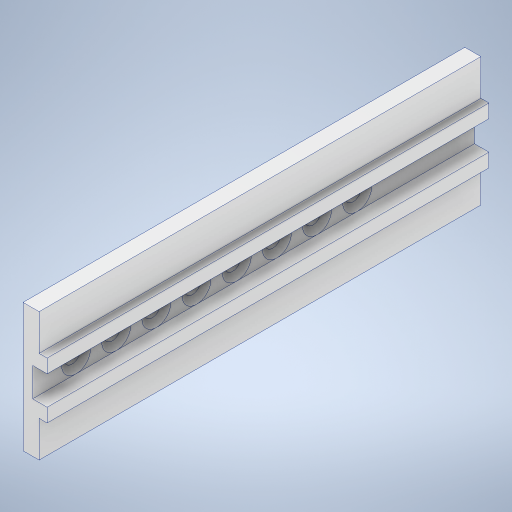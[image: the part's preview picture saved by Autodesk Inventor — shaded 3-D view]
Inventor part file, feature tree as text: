
AUTODESK INVENTOR PART (.ipt)
format: ipt  version: 2024 (Build 280153000, 153)  size: 330,240 bytes
history: native  units: mm
features: extrude x3, sketch x3, chamfer x1
ambient origin geometry x8: Origin, YZ Plane, XZ Plane, XY Plane, X Axis, Y Axis, Z Axis, Center Point
bodies: Solid1 (feature_tree)
feature tree (7):
  extrude  "Extrusion1"  Depth=160.0mm TaperAngle=0.0deg
  extrude  "Extrusion2"  Depth=25.0mm
  extrude  "Extrusion3"  Depth=45.0mm
  chamfer  "Chamfer1"  Distance=45.0mm
  sketch  "Sketch1"  dims[d0=550.0mm d1=160.0mm d2=0.0mm]
  sketch  "Sketch2"  dims[d4=25.0mm d5=25.0mm]
  sketch  "Sketch3"  dims[d6=10.0mm d7=45.0mm d8=45.0mm d9=18.0mm d10=36.0mm d11=80.0mm d12=80.0mm d13=150.0mm d14=0.0mm d15=30.0mm d16=90.0mm d18=50.0mm d19=10.0mm d21=10.0mm d23=25.0mm d24=0.0mm d25=8.0mm d26=5.0mm d27=45.0deg d28=39.130435mm]
